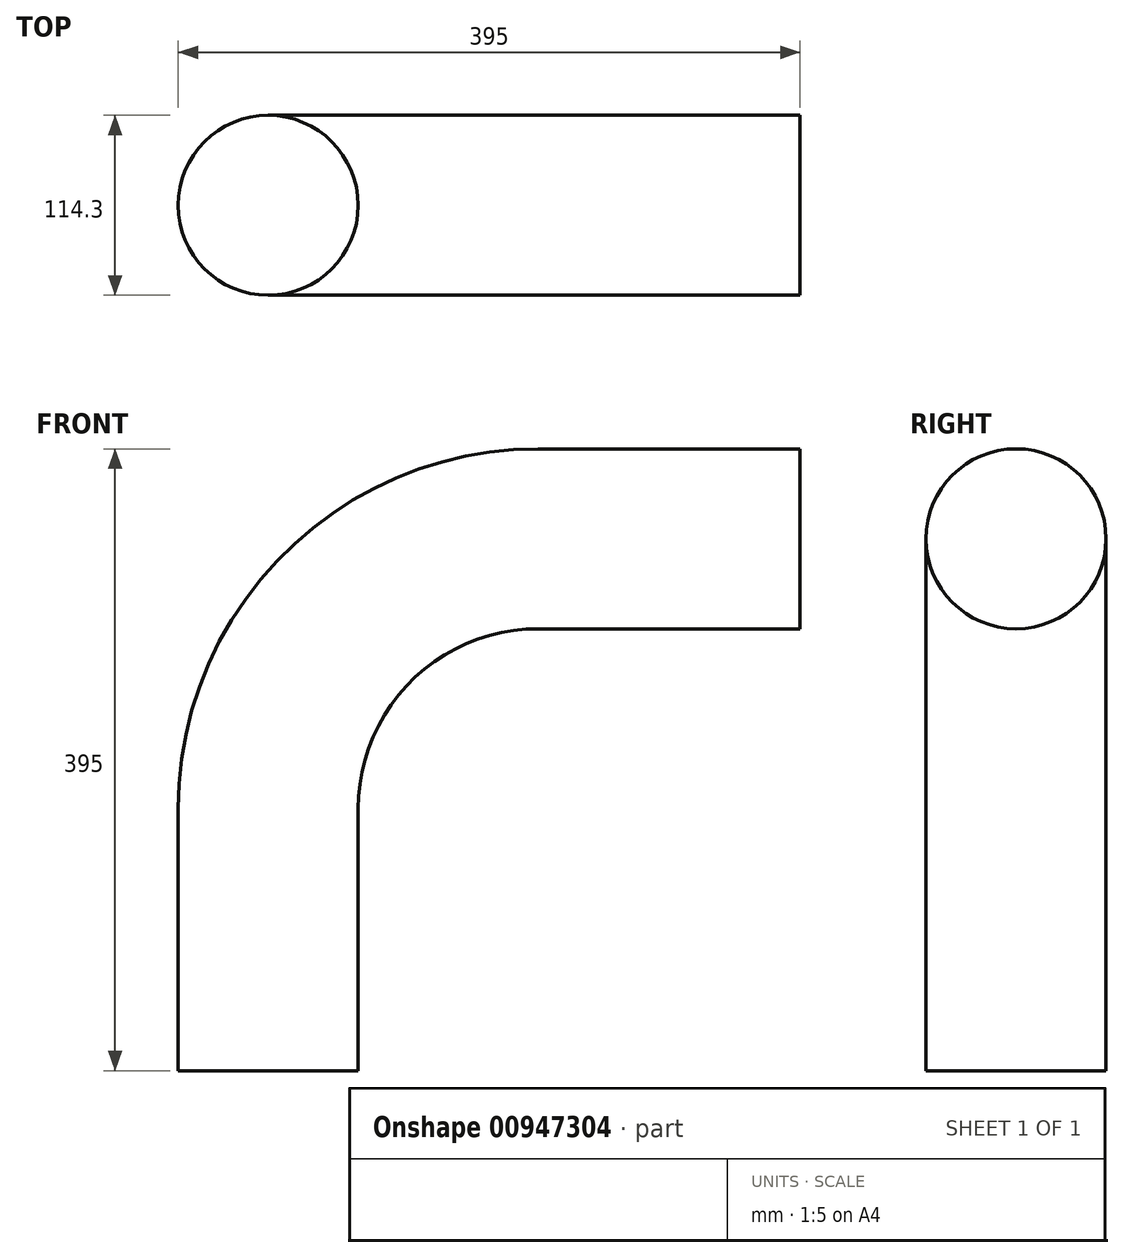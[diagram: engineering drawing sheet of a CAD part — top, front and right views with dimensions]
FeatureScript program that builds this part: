
annotation { "Feature Type Name" : "Feature", "Feature Type Description" : "" }
export const myFeature = defineFeature(function(context is Context, id is Id, definition is map)
    precondition{}
    {
        {
            var Q0;
            Q0=qCreatedBy(makeId("Top.planeOp"),FACE);
            var sketch = newSketch(context, id + "F0", { "sketchPlane" : qUnion([Q0])});
            skCircle(sketch, "E0", {"center": v(0, 0) * mm, "radius": 57.15 * mm});
            skSolve(sketch);
        }
        {
            var Q0;
            Q0=qCreatedBy(makeId("Front.planeOp"),FACE);
            var sketch = newSketch(context, id + "F1", { "sketchPlane" : qUnion([Q0])});
            skLineSegment(sketch, "E1", {"start": v(0, 0) * mm, "end": v(0, 166.45) * mm});
            skLineSegment(sketch, "E2", {"start": v(171.4, 337.85) * mm, "end": v(337.85, 337.85) * mm});
            skPoint(sketch, "E3.visualSharp", {"position": v(0, 337.85) * mm});
            skArc(sketch, "E3.filletArc", {"start": v(171.4, 337.85) * mm, "mid": v(50.2, 287.65) * mm, "end": v(0, 166.45) * mm});
            skSolve(sketch);
        }
        {
            var Q0;
            Q0=makeQuery(id+"F0.imprint","IMPRINT",FACE,{"disambiguationData":[TD([[makeQuery(id+"F0.imprint","IMPRINT",EDGE,{"derivedFrom":sQuery(id+"F0.wireOp",EDGE,"E0")}),1.0]])]});
            var Q1;
            Q1=sQuery(id+"F1.wireOp",EDGE,"E1");
            var Q2;
            Q2=sQuery(id+"F1.wireOp",EDGE,"E3.filletArc");
            var Q3;
            Q3=sQuery(id+"F1.wireOp",EDGE,"E2");
            sweep(context, id + "F2", {"profiles" : qUnion([Q0]), "path" : qUnion([Q1, Q2, Q3])});
        }
    });
